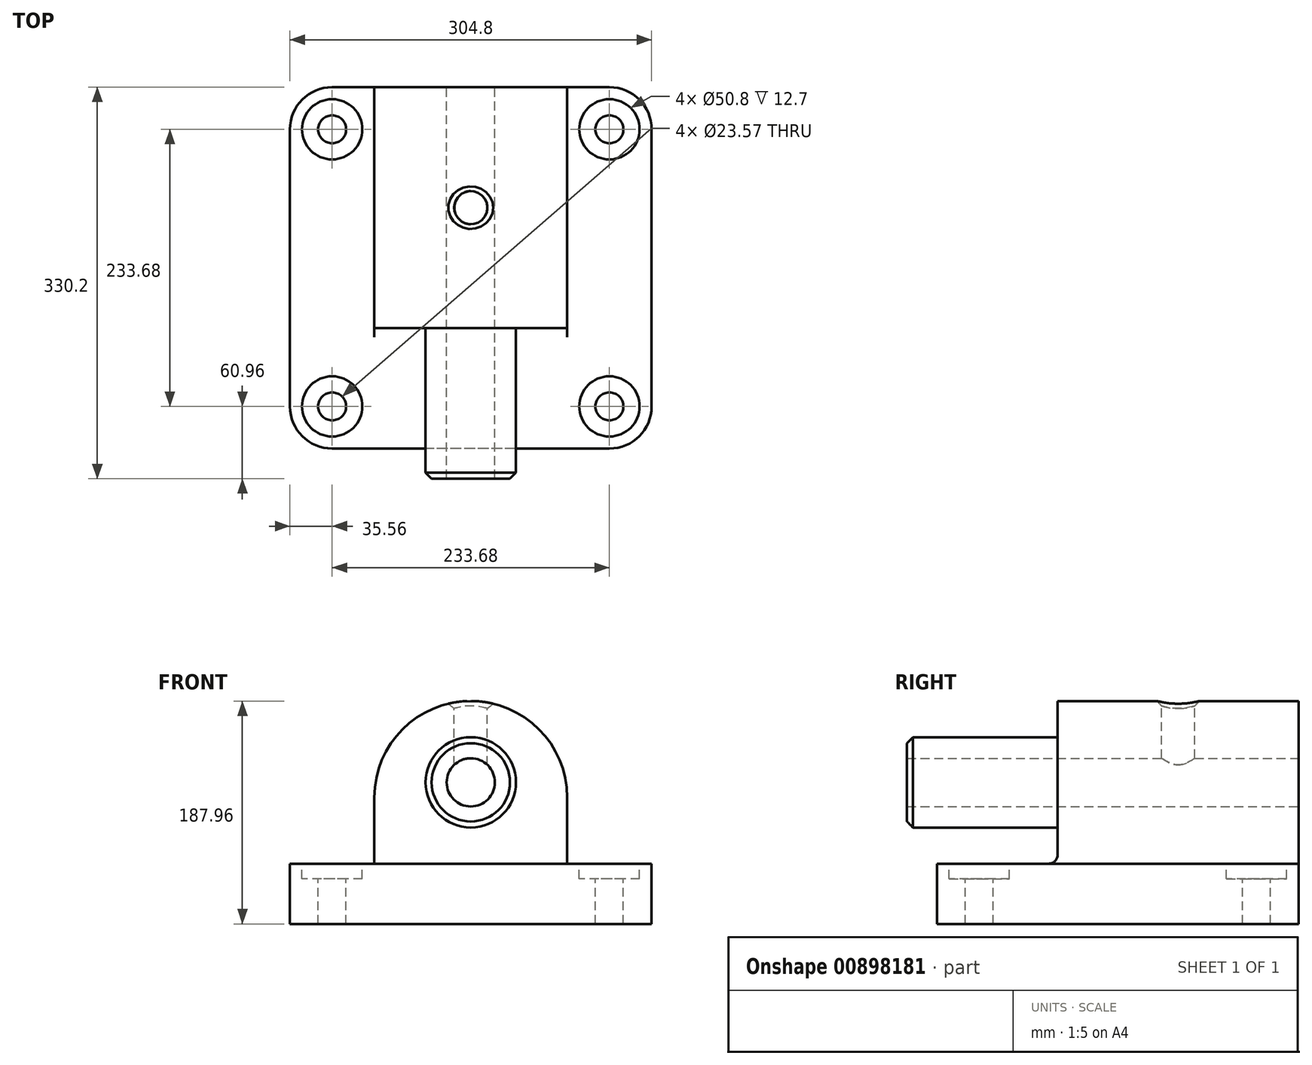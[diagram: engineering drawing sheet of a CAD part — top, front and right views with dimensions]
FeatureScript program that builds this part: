
annotation { "Feature Type Name" : "Feature", "Feature Type Description" : "" }
export const myFeature = defineFeature(function(context is Context, id is Id, definition is map)
    precondition{}
    {
        {
            var Q0;
            Q0=qCreatedBy(makeId("Top.planeOp"),FACE);
            var sketch = newSketch(context, id + "F0", { "sketchPlane" : qUnion([Q0])});
            skLineSegment(sketch, "E0.bottom", {"start": v(116.84, 152.4) * mm, "end": v(-116.84, 152.4) * mm});
            skLineSegment(sketch, "E0.top", {"start": v(116.84, -152.4) * mm, "end": v(-116.84, -152.4) * mm});
            skLineSegment(sketch, "E0.left", {"start": v(152.4, 116.84) * mm, "end": v(152.4, -116.84) * mm});
            skLineSegment(sketch, "E0.right", {"start": v(-152.4, 116.84) * mm, "end": v(-152.4, -116.84) * mm});
            skPoint(sketch, "E0.middle", {"position": v(0, 0) * mm});
            skPoint(sketch, "E1.visualSharp", {"position": v(-152.4, -152.4) * mm});
            skArc(sketch, "E1.filletArc", {"start": v(-152.4, -116.84) * mm, "mid": v(-141.98, -141.98) * mm, "end": v(-116.84, -152.4) * mm});
            skPoint(sketch, "E2.visualSharp", {"position": v(152.4, -152.4) * mm});
            skArc(sketch, "E2.filletArc", {"start": v(116.84, -152.4) * mm, "mid": v(141.98, -141.98) * mm, "end": v(152.4, -116.84) * mm});
            skPoint(sketch, "E3.visualSharp", {"position": v(152.4, 152.4) * mm});
            skArc(sketch, "E3.filletArc", {"start": v(152.4, 116.84) * mm, "mid": v(141.98, 141.98) * mm, "end": v(116.84, 152.4) * mm});
            skPoint(sketch, "E4.visualSharp", {"position": v(-152.4, 152.4) * mm});
            skArc(sketch, "E4.filletArc", {"start": v(-116.84, 152.4) * mm, "mid": v(-141.98, 141.98) * mm, "end": v(-152.4, 116.84) * mm});
            skSolve(sketch);
        }
        {
            var Q0;
            Q0=makeQuery(id+"F0.imprint","IMPRINT",FACE,{"disambiguationData":[TD([[makeQuery(id+"F0.imprint","IMPRINT",EDGE,{"derivedFrom":sQuery(id+"F0.wireOp",EDGE,"E0.bottom")}),1.0]])]});
            extrude(context, id + "F1", {"entities" : qUnion([Q0]), "depth" : 50.8 * mm, "offsetDistance" : 25.4 * mm});
        }
        {
            var Q0;
            Q0=makeQuery(id+"F1.opExtrude","CAP_FACE",FACE,{"disambiguationData":[OSD([sQuery(id+"F0.wireOp",EDGE,"E0.bottom"),sQuery(id+"F0.wireOp",EDGE,"E0.top"),sQuery(id+"F0.wireOp",EDGE,"E0.left"),sQuery(id+"F0.wireOp",EDGE,"E0.right"),sQuery(id+"F0.wireOp",EDGE,"E1.filletArc"),sQuery(id+"F0.wireOp",EDGE,"E2.filletArc"),sQuery(id+"F0.wireOp",EDGE,"E3.filletArc"),sQuery(id+"F0.wireOp",EDGE,"E4.filletArc")])],"isStart":false});
            var sketch = newSketch(context, id + "F2", { "sketchPlane" : qUnion([Q0])});
            skLineSegment(sketch, "E5.bottom", {"start": v(81.28, 152.4) * mm, "end": v(-81.28, 152.4) * mm});
            skLineSegment(sketch, "E5.top", {"start": v(81.28, -152.4) * mm, "end": v(-81.28, -152.4) * mm});
            skLineSegment(sketch, "E5.left", {"start": v(81.28, 152.4) * mm, "end": v(81.28, -152.4) * mm});
            skLineSegment(sketch, "E5.right", {"start": v(-81.28, 152.4) * mm, "end": v(-81.28, -152.4) * mm});
            skPoint(sketch, "E5.middle", {"position": v(0, 0) * mm});
            skSolve(sketch);
        }
        {
            var Q0;
            Q0 = qSketchRegion(id + "F2", true);
            var sketch = newSketch(context, id + "F3", { "sketchPlane" : qUnion([Q0])});
            skSolve(sketch);
        }
        {
            var Q0;
            Q0=makeQuery(id+"F3.imprint","IMPRINT",FACE,{"disambiguationData":[TD([[makeQuery(id+"F3.imprint","IMPRINT",EDGE,{"derivedFrom":makeQuery(id+"F2.imprint","IMPRINT",EDGE,{"derivedFrom":sQuery(id+"F2.wireOp",EDGE,"E5.bottom")})}),1.0]])]});
            extrude(context, id + "F4", {"entities" : qUnion([Q0]), "operationType" : NewBodyOperationType.ADD, "depth" : 137.16 * mm, "offsetDistance" : 25.4 * mm});
        }
        {
            var Q0;
            Q0=makeQuery(id+"F4.opExtrude","SWEPT_FACE",FACE,{"disambiguationData":[OSD([sQuery(id+"F2.wireOp",EDGE,"E5.left")])]});
            var sketch = newSketch(context, id + "F5", { "sketchPlane" : qUnion([Q0])});
            skLineSegment(sketch, "E6.bottom", {"start": v(-152.4, 50.8) * mm, "end": v(-50.8, 50.8) * mm});
            skLineSegment(sketch, "E6.top", {"start": v(-152.4, 187.96) * mm, "end": v(-50.8, 187.96) * mm});
            skLineSegment(sketch, "E6.left", {"start": v(-152.4, 50.8) * mm, "end": v(-152.4, 187.96) * mm});
            skLineSegment(sketch, "E6.right", {"start": v(-50.8, 50.8) * mm, "end": v(-50.8, 187.96) * mm});
            skSolve(sketch);
        }
        {
            var Q0;
            Q0 = qSketchRegion(id + "F5", true);
            extrude(context, id + "F6", {"entities" : qUnion([Q0]), "operationType" : NewBodyOperationType.REMOVE, "oppositeDirection" : true, "depth" : 309.63 * mm, "offsetDistance" : 25.4 * mm});
        }
        {
            var Q0;
            Q0=makeQuery(id+"F6.boolean.opBoolean","COPY",FACE,{"derivedFrom":makeQuery(id+"F6.opExtrude","SWEPT_FACE",FACE,{"disambiguationData":[OSD([sQuery(id+"F5.wireOp",EDGE,"E6.right")])]})});
            var sketch = newSketch(context, id + "F7", { "sketchPlane" : qUnion([Q0])});
            skCircle(sketch, "E7", {"center": v(0, 119.38) * mm, "radius": 38.1 * mm});
            skPoint(sketch, "E7.centerSnap0", {"position": v(81.28, 119.38) * mm});
            skPoint(sketch, "E7.centerSnap1", {"position": v(0, 187.96) * mm});
            skSolve(sketch);
        }
        {
            var Q0;
            Q0 = qSketchRegion(id + "F7", true);
            extrude(context, id + "F8", {"entities" : qUnion([Q0]), "operationType" : NewBodyOperationType.ADD, "depth" : 127 * mm, "offsetDistance" : 25.4 * mm});
        }
        {
            var Q0;
            Q0=makeQuery(id+"F8.opExtrude","CAP_EDGE",EDGE,{"disambiguationData":[OSD([sQuery(id+"F7.wireOp",EDGE,"E7")])],"isStart":false});
            chamfer(context, id + "F9", {"entities" : qUnion([Q0]), "width" : 5.08 * mm, "tangentPropagation" : true});
        }
        {
            var Q0;
            Q0=makeQuery(id+"F4.opExtrude","CAP_EDGE",EDGE,{"disambiguationData":[OSD([sQuery(id+"F2.wireOp",EDGE,"E5.left")])],"isStart":false});
            var Q1;
            Q1=makeQuery(id+"F4.opExtrude","CAP_EDGE",EDGE,{"disambiguationData":[OSD([sQuery(id+"F2.wireOp",EDGE,"E5.right")])],"isStart":false});
            fillet(context, id + "F10", {"entities" : qUnion([Q0, Q1]), "tangentPropagation" : true, "radius" : 81.28 * mm, "defaultsChanged" : true, "vertexSettings" : [], "allowEdgeOverflow" : false});
        }
        {
            var Q0;
            Q0=makeQuery(id+"F4.boolean.opBoolean","MERGE",FACE,{"derivedFrom":[makeQuery(id+"F1.opExtrude","SWEPT_FACE",FACE,{"disambiguationData":[OSD([sQuery(id+"F0.wireOp",EDGE,"E0.bottom")])]}),makeQuery(id+"F4.opExtrude","SWEPT_FACE",FACE,{"disambiguationData":[OSD([sQuery(id+"F2.wireOp",EDGE,"E5.bottom")])]})]});
            var sketch = newSketch(context, id + "F11", { "sketchPlane" : qUnion([Q0])});
            skCircle(sketch, "E8", {"center": v(0, 119.38) * mm, "radius": 20.32 * mm});
            skSolve(sketch);
        }
        {
            var Q0;
            Q0 = qSketchRegion(id + "F11", true);
            extrude(context, id + "F12", {"entities" : qUnion([Q0]), "operationType" : NewBodyOperationType.REMOVE, "oppositeDirection" : true, "depth" : 373.9 * mm, "offsetDistance" : 25.4 * mm});
        }
        {
            var Q0;
            {var subQ2=sQuery(id+"F2.wireOp",EDGE,"E5.left");Q0=makeQuery(id+"F2.imprint","IMPRINT",FACE,{"disambiguationData":[TD([[makeQuery(id+"F2.imprint","IMPRINT",EDGE,{"derivedFrom":subQ2}),1.0]])]});}
            var sketch = newSketch(context, id + "F13", { "sketchPlane" : qUnion([Q0])});
            skCircle(sketch, "E9", {"center": v(116.84, 116.84) * mm, "radius": 25.4 * mm});
            skCircle(sketch, "E10", {"center": v(116.84, -116.84) * mm, "radius": 25.4 * mm});
            skCircle(sketch, "E11", {"center": v(-116.84, 116.84) * mm, "radius": 25.4 * mm});
            skCircle(sketch, "E12", {"center": v(-116.84, -116.84) * mm, "radius": 25.4 * mm});
            skSolve(sketch);
        }
        {
            var Q0;
            Q0 = qSketchRegion(id + "F13", true);
            extrude(context, id + "F14", {"entities" : qUnion([Q0]), "operationType" : NewBodyOperationType.REMOVE, "oppositeDirection" : true, "depth" : 12.7 * mm, "offsetDistance" : 25.4 * mm});
        }
        {
            var Q0;
            {var subQ2=sQuery(id+"F2.wireOp",EDGE,"E5.left");Q0=makeQuery(id+"F2.imprint","IMPRINT",FACE,{"disambiguationData":[TD([[makeQuery(id+"F2.imprint","IMPRINT",EDGE,{"derivedFrom":subQ2}),1.0]])]});}
            var sketch = newSketch(context, id + "F15", { "sketchPlane" : qUnion([Q0])});
            skCircle(sketch, "E13", {"center": v(116.84, 116.84) * mm, "radius": 11.78 * mm});
            skCircle(sketch, "E14", {"center": v(116.84, -116.84) * mm, "radius": 11.78 * mm});
            skCircle(sketch, "E15", {"center": v(-116.84, 116.84) * mm, "radius": 11.78 * mm});
            skCircle(sketch, "E16", {"center": v(-116.84, -116.84) * mm, "radius": 11.78 * mm});
            skSolve(sketch);
        }
        {
            var Q0;
            Q0 = qSketchRegion(id + "F15", true);
            extrude(context, id + "F16", {"entities" : qUnion([Q0]), "operationType" : NewBodyOperationType.REMOVE, "oppositeDirection" : true, "depth" : 87.12 * mm, "offsetDistance" : 25.4 * mm});
        }
        {
            var Q0;
            Q0=makeQuery(id+"F2.imprint","IMPRINT",FACE,{"disambiguationData":[TD([[makeQuery(id+"F2.imprint","IMPRINT",EDGE,{"derivedFrom":sQuery(id+"F2.wireOp",EDGE,"E5.bottom")}),1.0]])]});
            cPlane(context, id + "F17", {"entities" : qUnion([Q0]), "cplaneType" : CPlaneType.OFFSET, "offset" : 137.16 * mm, "width" : 152.4 * mm, "height" : 152.4 * mm});
        }
        {
            var Q0;
            Q0=qCreatedBy(id+"F17.planeOp",FACE);
            var sketch = newSketch(context, id + "F18", { "sketchPlane" : qUnion([Q0])});
            skCircle(sketch, "E17", {"center": v(0, 50.8) * mm, "radius": 13.97 * mm});
            skSolve(sketch);
        }
        {
            var Q0;
            Q0 = qSketchRegion(id + "F18", true);
            extrude(context, id + "F19", {"entities" : qUnion([Q0]), "operationType" : NewBodyOperationType.REMOVE, "oppositeDirection" : true, "depth" : 63.25 * mm, "offsetDistance" : 25.4 * mm});
        }
        {
            var Q0;
            Q0=makeQuery(id+"F19.boolean.opBoolean","INTERSECT",EDGE,{"derivedFrom":[makeQuery(id+"F10.opFillet","BLEND_FACE",FACE,{"disambiguationData":[OSD([sQuery(id+"F2.wireOp",EDGE,"E5.left")])]}),makeQuery(id+"F19.opExtrude","SWEPT_FACE",FACE,{"disambiguationData":[OSD([sQuery(id+"F18.wireOp",EDGE,"E17")])]})]});
            chamfer(context, id + "F20", {"entities" : qUnion([Q0]), "width" : 5.08 * mm, "tangentPropagation" : true});
        }
        {
            var Q0;
            Q0=makeQuery(id+"F4.opExtrude","CAP_EDGE",EDGE,{"disambiguationData":[OSD([sQuery(id+"F2.wireOp",EDGE,"E5.left")])],"isStart":true});
            var Q1;
            Q1=makeQuery(id+"F6.boolean.opBoolean","COPY",EDGE,{"derivedFrom":makeQuery(id+"F6.opExtrude","SWEPT_EDGE",EDGE,{"disambiguationData":[OSD([sQuery(id+"F2.wireOp",EDGE,"E5.left"),sQuery(id+"F5.wireOp",EDGE,"E6.bottom"),sQuery(id+"F5.wireOp",EDGE,"E6.right")])]})});
            var Q2;
            Q2=makeQuery(id+"F6.boolean.opBoolean","COPY",EDGE,{"derivedFrom":makeQuery(id+"F6.opExtrude","CAP_EDGE",EDGE,{"disambiguationData":[OSD([sQuery(id+"F5.wireOp",EDGE,"E6.right")])],"isStart":true})});
            var Q3;
            Q3=makeQuery(id+"F8.opExtrude","CAP_EDGE",EDGE,{"disambiguationData":[OSD([sQuery(id+"F7.wireOp",EDGE,"E7")])],"isStart":true});
            fillet(context, id + "F21", {"entities" : qUnion([Q0, Q1, Q2, Q3]), "tangentPropagation" : true, "radius" : 7.62 * mm, "defaultsChanged" : true, "vertexSettings" : [], "allowEdgeOverflow" : false});
        }
    });
